# Revit family: Afb. Krone. + Afb. Kor. + Stikk.
name_source: partatom
category: Electrical Fixtures
units: mm (PartAtom-declared; Revit-internal decimal feet)

## family parameters
Cut with Voids When Loaded = No
Host = Face
Maintain Annotation Orientation = Yes
Part Type = Switch
Room Calculation Point = No
Round Connector Dimension = Use Diameter
Shared = No

## types (1)
- Baseline 63
    Baseline 50 = No
    Baseline 63 = Yes
    Cone = No
    Cut Depth = 2 mm  [stored 0.00656168 ft]
    Dase = No
    Dase Height = 73 mm  [stored 0.239501 ft]
    Dase Width = 46 mm  [stored 0.150919 ft]
    Default Elevation = 1100 mm
    Frame = LK Frame
    Frame Size = 63 mm  [stored 0.206693 ft]
    Frame Type = 2
    GoGetNo = 1615
    Height Type = 2 mm  [stored 0.00656168 ft]
    IsBaseline = Yes
    IsSoftline = No
    Modul Height = 77 mm  [stored 0.252625 ft]
    Modul Width = 50 mm  [stored 0.164042 ft]
    Outlet Placement = 9 mm  [stored 0.0295276 ft]
    RFT = 2
    Ramme = Baseline 63
    Text = Text
    Wall Cut Depth = 50 mm  [stored 0.164042 ft]
    Width Type = 1 mm  [stored 0.00328084 ft]

note: [stored X ft] marks values corroborated as IEEE doubles in the binary element streams (Revit-internal decimal feet)

## geometry (parser evidence)
native form markers: Sweep x30
no freeform markers — native parametric forms only
